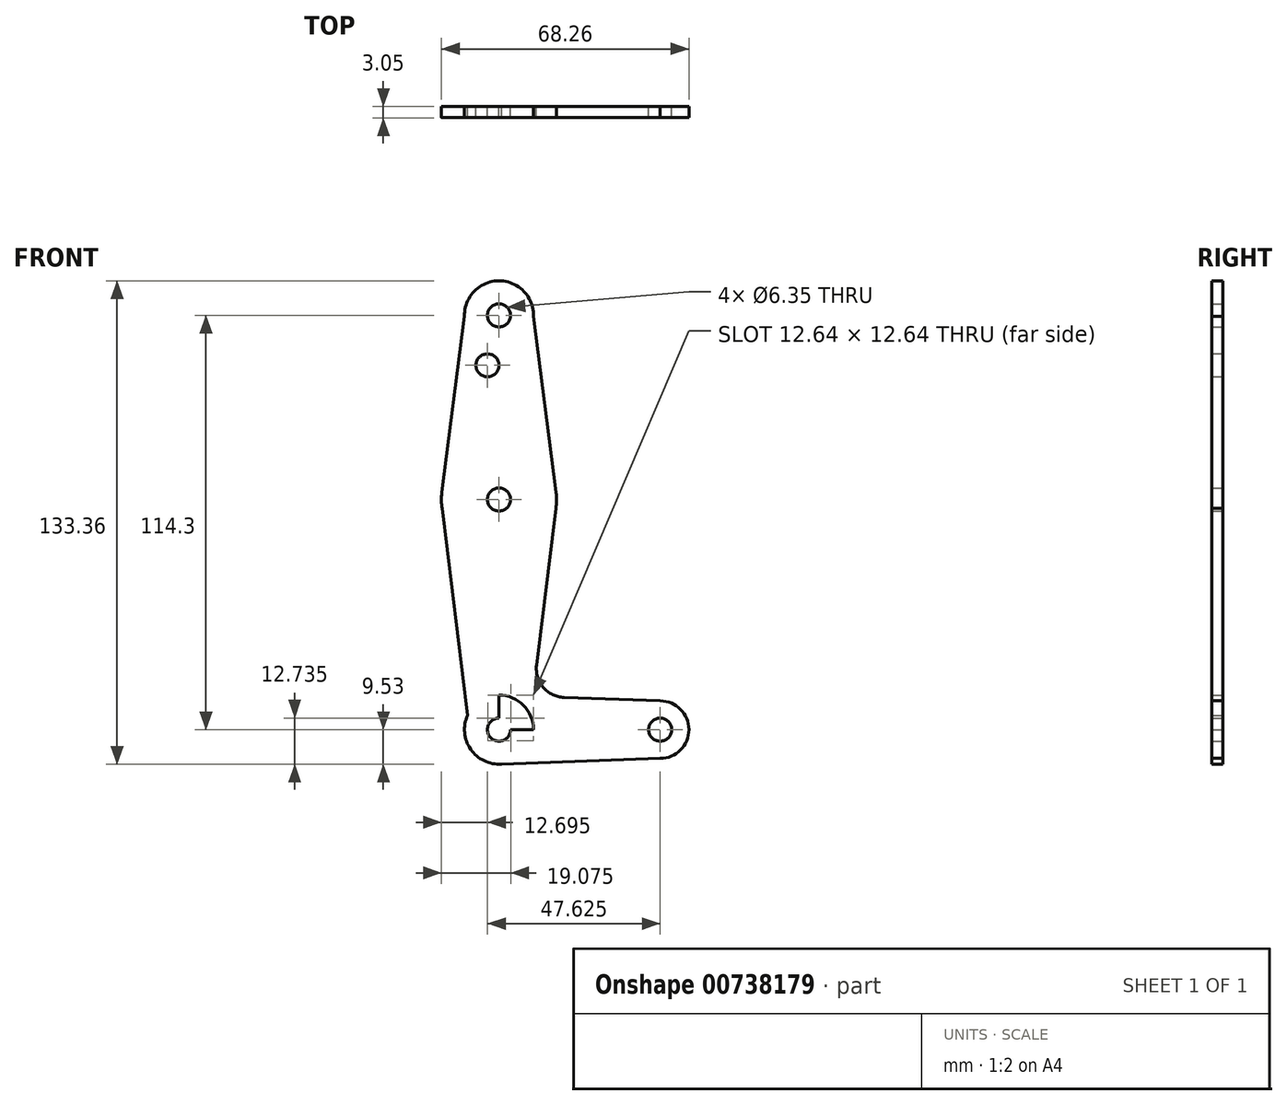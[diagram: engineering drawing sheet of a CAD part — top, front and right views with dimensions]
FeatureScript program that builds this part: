
annotation { "Feature Type Name" : "Feature", "Feature Type Description" : "" }
export const myFeature = defineFeature(function(context is Context, id is Id, definition is map)
    precondition{}
    {
        {
            var Q0;
            Q0=qCreatedBy(makeId("Front.planeOp"),FACE);
            var sketch = newSketch(context, id + "F0", { "sketchPlane" : qUnion([Q0])});
            skLineSegment(sketch, "E0", {"start": v(0, 0) * mm, "end": v(0, 63.5) * mm});
            skLineSegment(sketch, "E1", {"start": v(0, 63.5) * mm, "end": v(0, 114.3) * mm});
            skLineSegment(sketch, "E2", {"start": v(0, 0) * mm, "end": v(44.45, 0) * mm});
            skCircle(sketch, "E3", {"center": v(0, 114.3) * mm, "radius": 9.53 * mm});
            skCircle(sketch, "E4", {"center": v(0, 63.5) * mm, "radius": 15.88 * mm});
            skCircle(sketch, "E5", {"center": v(0, 0) * mm, "radius": 9.53 * mm});
            skCircle(sketch, "E6", {"center": v(44.45, 0) * mm, "radius": 7.94 * mm});
            skLineSegment(sketch, "E7", {"start": v(-9.52, 114.03) * mm, "end": v(-15.75, 65.52) * mm});
            skLineSegment(sketch, "E8", {"start": v(9.52, 114.03) * mm, "end": v(15.75, 65.52) * mm});
            skLineSegment(sketch, "E9", {"start": v(-15.7, 61.13) * mm, "end": v(-8.65, 3.98) * mm});
            skLineSegment(sketch, "E10", {"start": v(15.7, 61.13) * mm, "end": v(10.36, 17.8) * mm});
            skLineSegment(sketch, "E11", {"start": v(17.96, 8.88) * mm, "end": v(44.45, 7.94) * mm});
            skLineSegment(sketch, "E12", {"start": v(0, -9.52) * mm, "end": v(44.45, -7.94) * mm});
            skCircle(sketch, "E13", {"center": v(-3.18, 100.52) * mm, "radius": 3.18 * mm});
            skCircle(sketch, "E14", {"center": v(0, 114.3) * mm, "radius": 3.18 * mm});
            skCircle(sketch, "E15", {"center": v(0, 63.5) * mm, "radius": 3.18 * mm});
            skCircle(sketch, "E16", {"center": v(0, 0) * mm, "radius": 3.18 * mm});
            skCircle(sketch, "E17", {"center": v(44.45, 0) * mm, "radius": 3.18 * mm});
            skPoint(sketch, "E18.newPointA", {"position": v(8.65, 3.98) * mm});
            skArc(sketch, "E18.filletArc", {"start": v(10.36, 17.8) * mm, "mid": v(12.2, 11.67) * mm, "end": v(17.96, 8.88) * mm});
            skSolve(sketch);
        }
        {
            var Q0;
            Q0 = qSketchRegion(id + "F0", true);
            extrude(context, id + "F1", {"entities" : qUnion([Q0]), "depth" : 3.05 * mm, "offsetDistance" : 25.4 * mm});
        }
    });
